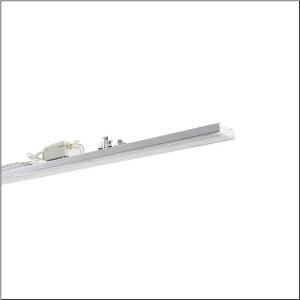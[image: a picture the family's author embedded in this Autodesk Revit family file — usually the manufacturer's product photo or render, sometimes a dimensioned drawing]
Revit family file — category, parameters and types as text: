
# Revit family: licross_r__21_recessed_mo_52te147n48xg_9933
name_source: partatom
category: Lighting Fixtures
units: mm (PartAtom-declared; Revit-internal decimal feet)

## family parameters
Cut with Voids When Loaded = No
Host = Face
Light Source = No
Part Type = Normal
Room Calculation Point = No
Round Connector Dimension = Use Diameter
Shared = No

## types (1)
- Licross® 21 Recessed MO (1 x LED, 8120 lm, 47.9 W, 4000K)
    Apparent Load = 48 VA
    CIE Flux Codes = 56 84 97 100 100
    Color Rendering = 80
    Color Temperature = 4000K
    Default Elevation = 1800 mm
    Description = Licross® 21 Recessed MO, luminaire insert, of sheet steel, galvanised, coil coated, white, length: 1.500mm, width: 66mm, height: 67mm, LED rated luminous flux: 8.120lm, light colour: 840, control gear: ON/OFF, with plug, 3-pole, with phase selection, mains connection: 220..240V, AC, 50/60Hz, rated input power: 48W, halogen-free wiring, primary light control with lens, of plastic, primary optical cover: cover, of PMMA, light emission: direct distribution, primary light characteristic: asymmetric, protection rating (complete): IP54, insulation class (complete): insulation class I (protective earthing), certification: CE, ENEC, VDE, UKCA, protection symbol: D if used in an environment with non-conductive dust loads with corresponding accessories, impact resistance: IK06, permissible ambient temperature for indoor applications: -35..+40°C, corresponds to IFS (International Featured Standards) requirements for safety and quality in the food industry, reducing of maximum allowable ambient temperature of 5°C with ceiling mounting, LABS conformity tested according to VDMA 24364:2018-05, packaging unit: 1 piece
    Height = 58 mm
    Lamp = 1 x LED
    Lamp Light Flux = 8120 lm
    Lamp Power = 47.9 W
    Lamp count = 1
    Length = 1500 mm
    Luminous efficacy = 170 lm/W
    Manufacturer = Siteco
    ModVariant = No
    Model = 52TE147N48XG
    Mounting Place = Ceiling
    Mounting Type = Pendant
    Number of Poles = 1
    OnlyDefault = Yes
    Power Factor = 1
    Product Name = Licross® 21 Recessed MO
    Product group = luminaire insert
    ProductGroupID = 901
    Protection Class = Protection class I
    Protection Degree = IP 54
    RLX_Detail_Level = 1
    RLX_Emergency_Light_Flux = 0 lm
    RLX_Emergency_Type = 0
    RLX_Emergency_Type_DB = No
    RlxData = <blob elided: 21361 chars, md5=3181fff2>
    Socket = socket
    Standby Power = 0 W
    System Light Flux = 8120 lm
    System Power = 48 W
    Type Comments = Product without accessories
    Type Image = l_1296930.jpg
    URL = http://relux.com
    VarID = ---
    Voltage = 0 V
    Weight = 0.00 kg
    Width = 66 mm

## geometry (parser evidence)
native form markers: Blend x4, Sweep x11
no freeform markers — native parametric forms only
